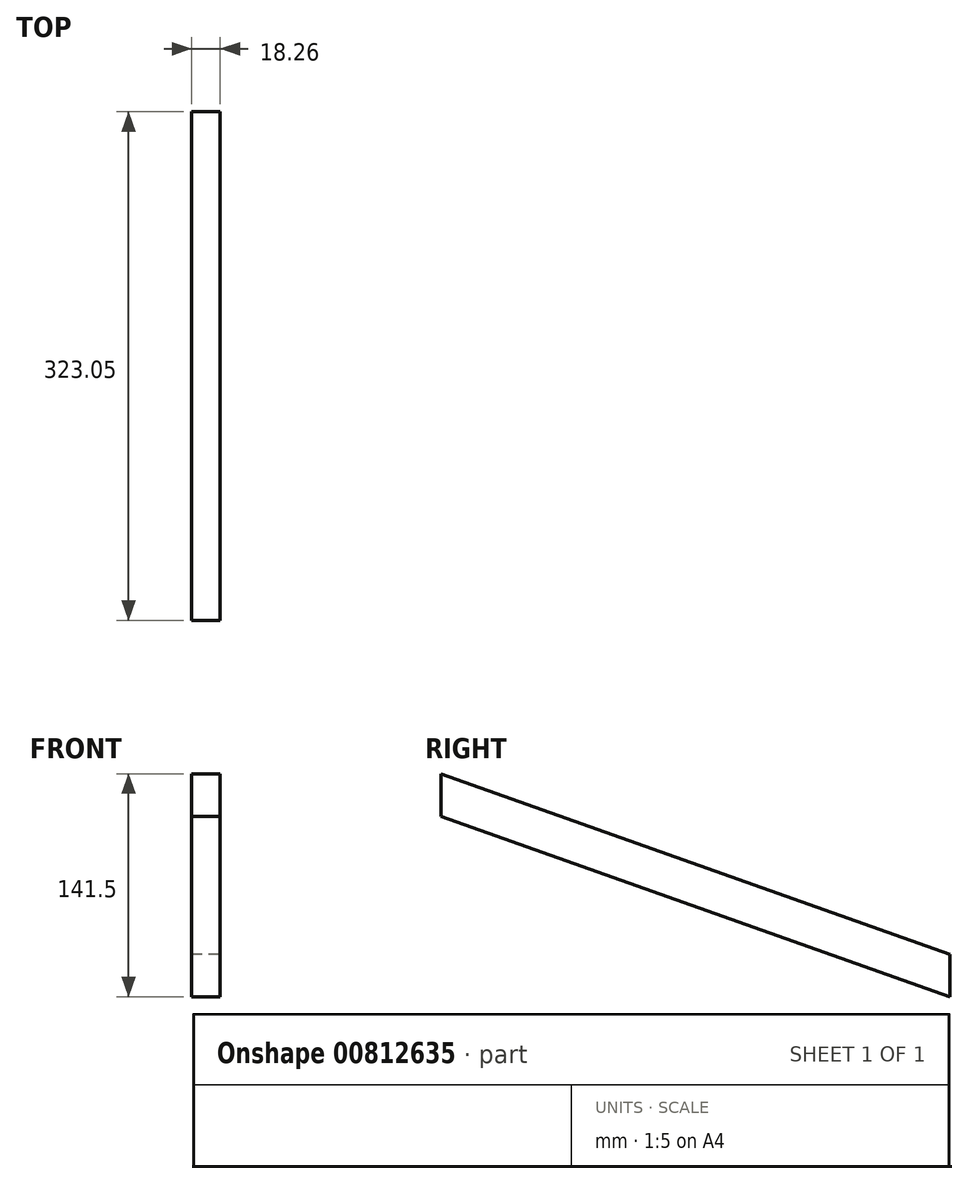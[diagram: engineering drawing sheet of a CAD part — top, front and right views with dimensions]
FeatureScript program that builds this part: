
annotation { "Feature Type Name" : "Feature", "Feature Type Description" : "" }
export const myFeature = defineFeature(function(context is Context, id is Id, definition is map)
    precondition{}
    {
        {
            var Q0;
            Q0=qCreatedBy(makeId("Right.planeOp"),FACE);
            var sketch = newSketch(context, id + "F0", { "sketchPlane" : qUnion([Q0])});
            skLineSegment(sketch, "E0", {"start": v(-138.66, -12.75) * mm, "end": v(-138.66, -114.35) * mm});
            skLineSegment(sketch, "E1", {"start": v(-138.66, -114.35) * mm, "end": v(147.88, -114.35) * mm});
            skLineSegment(sketch, "E2", {"start": v(147.88, -114.35) * mm, "end": v(-138.66, -12.75) * mm});
            skSolve(sketch);
        }
        {
            var Q0;
            Q0=qCreatedBy(makeId("Right.planeOp"),FACE);
            var sketch = newSketch(context, id + "F1", { "sketchPlane" : qUnion([Q0])});
            skLineSegment(sketch, "E3", {"start": v(-35.75, 12.33) * mm, "end": v(-35.75, -14.62) * mm});
            skLineSegment(sketch, "E4", {"start": v(-35.75, -14.62) * mm, "end": v(287.3, -129.17) * mm});
            skLineSegment(sketch, "E5", {"start": v(287.3, -129.17) * mm, "end": v(287.3, -102.22) * mm});
            skLineSegment(sketch, "E6", {"start": v(287.3, -102.22) * mm, "end": v(-35.75, 12.33) * mm});
            skSolve(sketch);
        }
        {
            var Q0;
            Q0=qSketchRegion(id+"F1",true);
            extrude(context, id + "F2", {"entities" : qUnion([Q0]), "depth" : 18.26 * mm, "offsetDistance" : 25.4 * mm});
        }
    });
